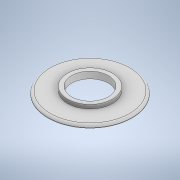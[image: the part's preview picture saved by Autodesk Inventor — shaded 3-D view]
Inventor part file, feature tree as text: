
AUTODESK INVENTOR PART (.ipt)
format: ipt  version: 2021 (Build 250183000, 183)  size: 124,416 bytes
history: native  units: mm
features: extrude x2, sketch x1, fillet x1
ambient origin geometry x8: Origin, YZ Plane, XZ Plane, XY Plane, X Axis, Y Axis, Z Axis, Center Point
bodies: Solid1 (feature_tree)
feature tree (4):
  sketch  "Sketch1"  dims[d0=45.5mm d1=104.0mm d2=55.5mm d3=4.75mm d4=0.0mm d5=3.5mm d6=0.0mm d7=3.0mm]
  extrude  "Extrusion1"  Depth=3.0mm
  extrude  "Extrusion2"  Depth=3.0mm
  fillet  "Fillet1"  Radius=4.75mm
